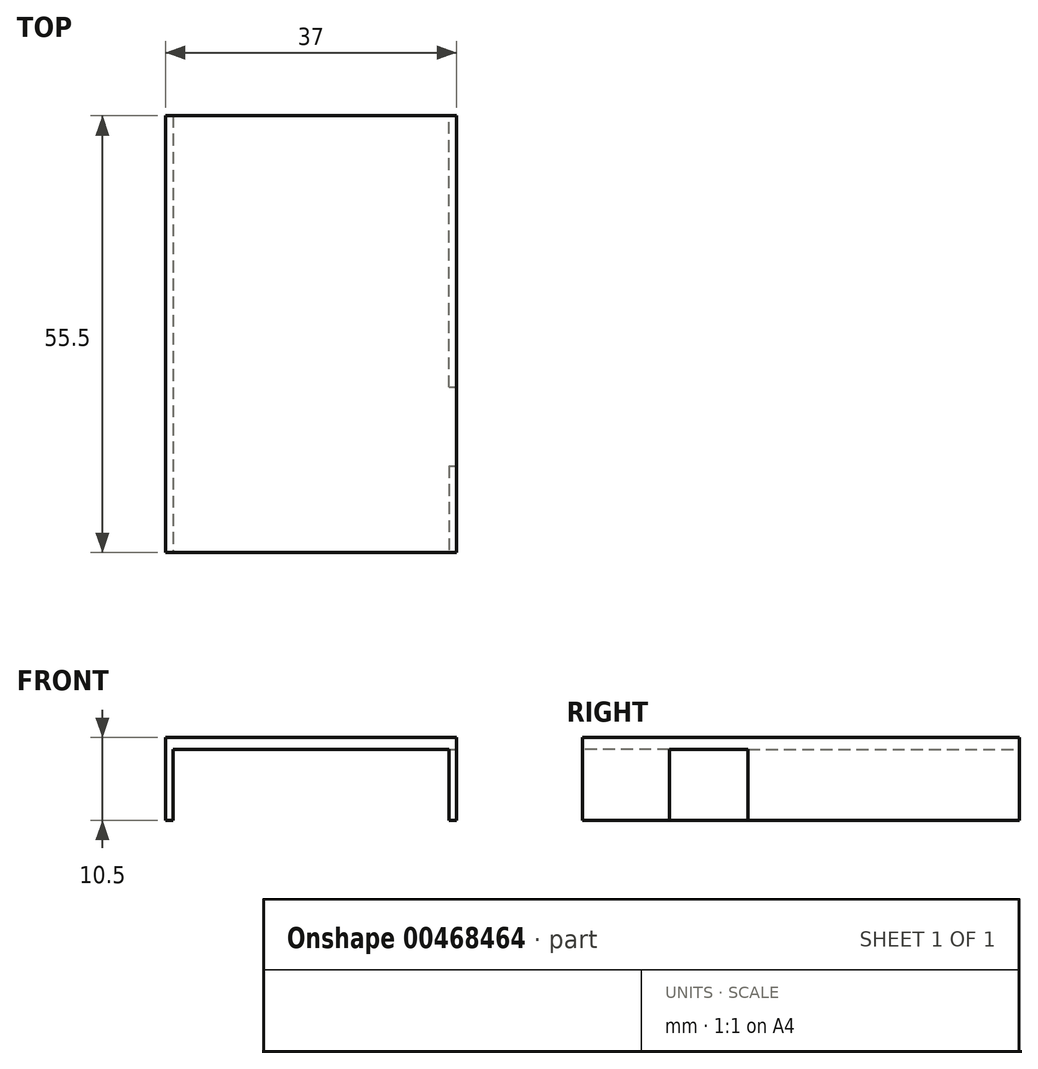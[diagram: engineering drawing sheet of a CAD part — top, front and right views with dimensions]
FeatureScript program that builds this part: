
annotation { "Feature Type Name" : "Feature", "Feature Type Description" : "" }
export const myFeature = defineFeature(function(context is Context, id is Id, definition is map)
    precondition{}
    {
        {
            var Q0;
            Q0=qCreatedBy(makeId("Top.planeOp"),FACE);
            var sketch = newSketch(context, id + "F0", { "sketchPlane" : qUnion([Q0])});
            skLineSegment(sketch, "E0", {"start": v(0, 26.75) * mm, "end": v(-17.5, 26.75) * mm});
            skLineSegment(sketch, "E1", {"start": v(-17.5, 26.75) * mm, "end": v(-17.5, 0) * mm});
            skLineSegment(sketch, "E2", {"start": v(-17.5, 0) * mm, "end": v(-17.5, -26.75) * mm});
            skLineSegment(sketch, "E3", {"start": v(-17.5, -26.75) * mm, "end": v(0, -26.75) * mm});
            skLineSegment(sketch, "E4", {"start": v(0, -27.75) * mm, "end": v(-18.5, -27.75) * mm});
            skLineSegment(sketch, "E5", {"start": v(-18.5, -27.75) * mm, "end": v(-18.5, 27.75) * mm});
            skLineSegment(sketch, "E6", {"start": v(-18.5, 27.75) * mm, "end": v(0, 27.75) * mm});
            skLineSegment(sketch, "E7.MirrorCS", {"start": v(17.5, -26.75) * mm, "end": v(0, -26.75) * mm});
            skLineSegment(sketch, "E8.MirrorCS", {"start": v(17.5, 0) * mm, "end": v(17.5, -26.75) * mm});
            skLineSegment(sketch, "E9.MirrorCS", {"start": v(0, -27.75) * mm, "end": v(18.5, -27.75) * mm});
            skLineSegment(sketch, "E10.MirrorCS", {"start": v(0, 26.75) * mm, "end": v(17.5, 26.75) * mm});
            skLineSegment(sketch, "E11.MirrorCS", {"start": v(18.5, 27.75) * mm, "end": v(0, 27.75) * mm});
            skLineSegment(sketch, "E12.MirrorCS", {"start": v(18.5, -27.75) * mm, "end": v(18.5, 27.75) * mm});
            skLineSegment(sketch, "E13.MirrorCS", {"start": v(17.5, 26.75) * mm, "end": v(17.5, 0) * mm});
            skLineSegment(sketch, "E14", {"start": v(-17.5, 26.75) * mm, "end": v(-17.5, 27.75) * mm});
            skLineSegment(sketch, "E15", {"start": v(17.5, 26.75) * mm, "end": v(17.5, 27.75) * mm});
            skLineSegment(sketch, "E16", {"start": v(-17.5, -26.75) * mm, "end": v(-17.5, -27.75) * mm});
            skLineSegment(sketch, "E17", {"start": v(17.5, -26.75) * mm, "end": v(17.5, -27.75) * mm});
            skLineSegment(sketch, "E18", {"start": v(17.5, -16.75) * mm, "end": v(18.5, -16.75) * mm});
            skLineSegment(sketch, "E19", {"start": v(17.5, -6.75) * mm, "end": v(18.5, -6.75) * mm});
            skSolve(sketch);
        }
        {
            var Q0;
            Q0=makeQuery(id+"F0.imprint","IMPRINT",FACE,{"disambiguationData":[TD([[makeQuery(id+"F0.imprint","IMPRINT",EDGE,{"derivedFrom":sQuery(id+"F0.wireOp",EDGE,"E0")}),-1.0]])]});
            var Q1;
            Q1=makeQuery(id+"F0.imprint","IMPRINT",FACE,{"disambiguationData":[TD([[makeQuery(id+"F0.imprint","IMPRINT",EDGE,{"derivedFrom":sQuery(id+"F0.wireOp",EDGE,"E1")}),-1.0]])]});
            var Q2;
            Q2=makeQuery(id+"F0.imprint","IMPRINT",FACE,{"disambiguationData":[TD([[makeQuery(id+"F0.imprint","IMPRINT",EDGE,{"derivedFrom":sQuery(id+"F0.wireOp",EDGE,"E0")}),1.0]])]});
            var Q3;
            Q3=makeQuery(id+"F0.imprint","IMPRINT",FACE,{"disambiguationData":[TD([[makeQuery(id+"F0.imprint","IMPRINT",EDGE,{"derivedFrom":sQuery(id+"F0.wireOp",EDGE,"E3")}),-1.0]])]});
            var Q4;
            {var subQ0=sQuery(id+"F0.wireOp",EDGE,"E13.MirrorCS");Q4=makeQuery(id+"F0.imprint","IMPRINT",FACE,{"disambiguationData":[TD([[makeQuery(id+"F0.imprint","IMPRINT",EDGE,{"derivedFrom":subQ0}),1.0]])]});}
            var Q5;
            {var subQ0=sQuery(id+"F0.wireOp",EDGE,"E17");Q5=makeQuery(id+"F0.imprint","IMPRINT",FACE,{"disambiguationData":[TD([[makeQuery(id+"F0.imprint","IMPRINT",EDGE,{"derivedFrom":subQ0}),1.0]])]});}
            var Q6;
            {var subQ0=sQuery(id+"F0.wireOp",EDGE,"E18");Q6=makeQuery(id+"F0.imprint","IMPRINT",FACE,{"disambiguationData":[TD([[makeQuery(id+"F0.imprint","IMPRINT",EDGE,{"derivedFrom":subQ0}),1.0]])]});}
            extrude(context, id + "F1", {"entities" : qUnion([Q0, Q1, Q2, Q3, Q4, Q5, Q6]), "depth" : 1.5 * mm, "offsetDistance" : 25 * mm});
        }
        {
            var Q0;
            Q0=makeQuery(id+"F0.imprint","IMPRINT",FACE,{"disambiguationData":[TD([[makeQuery(id+"F0.imprint","IMPRINT",EDGE,{"derivedFrom":sQuery(id+"F0.wireOp",EDGE,"E1")}),-1.0]])]});
            var Q1;
            {var subQ0=sQuery(id+"F0.wireOp",EDGE,"E13.MirrorCS");Q1=makeQuery(id+"F0.imprint","IMPRINT",FACE,{"disambiguationData":[TD([[makeQuery(id+"F0.imprint","IMPRINT",EDGE,{"derivedFrom":subQ0}),1.0]])]});}
            var Q2;
            {var subQ0=sQuery(id+"F0.wireOp",EDGE,"E17");Q2=makeQuery(id+"F0.imprint","IMPRINT",FACE,{"disambiguationData":[TD([[makeQuery(id+"F0.imprint","IMPRINT",EDGE,{"derivedFrom":subQ0}),1.0]])]});}
            extrude(context, id + "F2", {"entities" : qUnion([Q0, Q1, Q2]), "operationType" : NewBodyOperationType.ADD, "oppositeDirection" : true, "depth" : 9 * mm, "offsetDistance" : 25 * mm});
        }
    });
